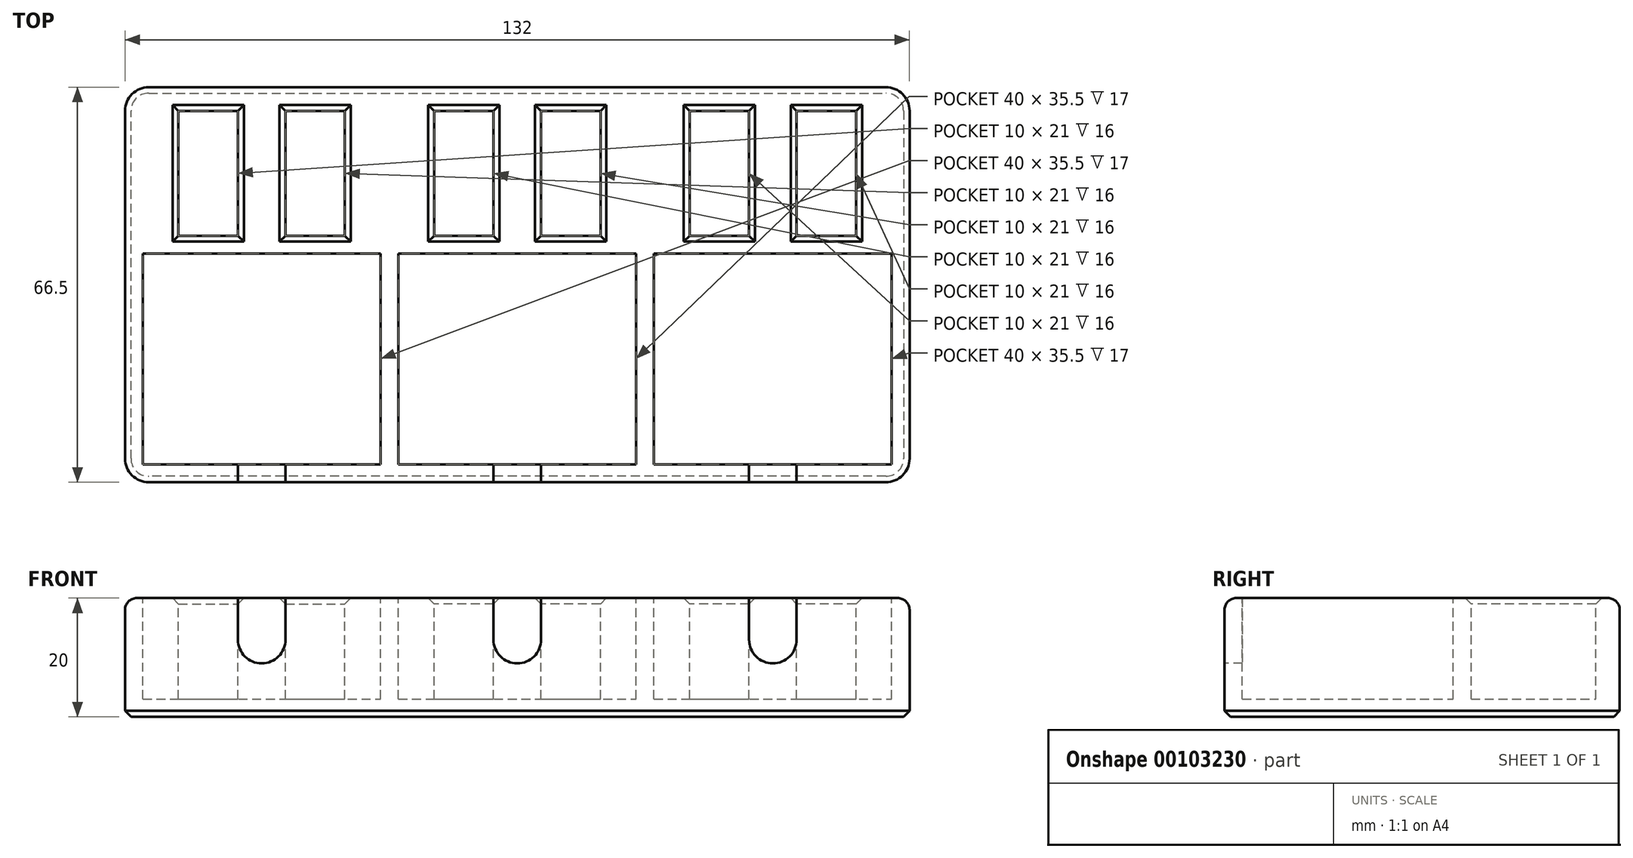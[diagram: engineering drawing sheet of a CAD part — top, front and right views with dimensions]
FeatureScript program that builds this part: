
annotation { "Feature Type Name" : "Feature", "Feature Type Description" : "" }
export const myFeature = defineFeature(function(context is Context, id is Id, definition is map)
    precondition{}
    {
        {
            var Q0;
            Q0=qCreatedBy(makeId("Top.planeOp"),FACE);
            var sketch = newSketch(context, id + "F0", { "sketchPlane" : qUnion([Q0])});
            skLineSegment(sketch, "E0.bottom", {"start": v(-67.44, -14.2) * mm, "end": v(-57.44, -14.2) * mm});
            skLineSegment(sketch, "E0.top", {"start": v(-67.44, -35.2) * mm, "end": v(-57.44, -35.2) * mm});
            skLineSegment(sketch, "E0.left", {"start": v(-67.44, -14.2) * mm, "end": v(-67.44, -35.2) * mm});
            skLineSegment(sketch, "E0.right", {"start": v(-57.44, -14.2) * mm, "end": v(-57.44, -35.2) * mm});
            skLineSegment(sketch, "E1.bottom", {"start": v(-73.44, 24.3) * mm, "end": v(-33.44, 24.3) * mm});
            skLineSegment(sketch, "E1.top", {"start": v(-73.44, -11.2) * mm, "end": v(-33.44, -11.2) * mm});
            skLineSegment(sketch, "E1.left", {"start": v(-73.44, 24.3) * mm, "end": v(-73.44, -11.2) * mm});
            skLineSegment(sketch, "E1.right", {"start": v(-33.44, 24.3) * mm, "end": v(-33.44, -11.2) * mm});
            skLineSegment(sketch, "E2", {"start": v(-53.44, 24.3) * mm, "end": v(-53.44, -11.2) * mm, "construction": true});
            skLineSegment(sketch, "E3", {"start": v(-62.44, -14.2) * mm, "end": v(-62.44, -35.2) * mm, "construction": true});
            skLineSegment(sketch, "E4", {"start": v(-62.44, 24.3) * mm, "end": v(-62.44, -11.2) * mm, "construction": true});
            skLineSegment(sketch, "E5", {"start": v(-44.44, 24.3) * mm, "end": v(-44.44, -11.2) * mm, "construction": true});
            skLineSegment(sketch, "E6", {"start": v(-62.44, -11.2) * mm, "end": v(-62.44, -14.2) * mm, "construction": true});
            skLineSegment(sketch, "E7", {"start": v(-44.44, -11.2) * mm, "end": v(-44.44, -14.2) * mm, "construction": true});
            skLineSegment(sketch, "E8.bottom", {"start": v(-49.44, -14.2) * mm, "end": v(-39.44, -14.2) * mm});
            skLineSegment(sketch, "E8.top", {"start": v(-49.44, -35.2) * mm, "end": v(-39.44, -35.2) * mm});
            skLineSegment(sketch, "E8.left", {"start": v(-49.44, -14.2) * mm, "end": v(-49.44, -35.2) * mm});
            skLineSegment(sketch, "E8.right", {"start": v(-39.44, -14.2) * mm, "end": v(-39.44, -35.2) * mm});
            skLineSegment(sketch, "E9", {"start": v(-44.44, -35.2) * mm, "end": v(-44.44, -14.2) * mm, "construction": true});
            skLineSegment(sketch, "E10.1.0.0", {"start": v(3.56, -14.2) * mm, "end": v(3.56, -35.2) * mm});
            skLineSegment(sketch, "E10.1.0.1", {"start": v(-10.44, 24.3) * mm, "end": v(-10.44, -11.2) * mm, "construction": true});
            skLineSegment(sketch, "E10.1.0.2", {"start": v(9.56, 24.3) * mm, "end": v(9.56, -11.2) * mm});
            skLineSegment(sketch, "E10.1.0.3", {"start": v(-1.44, -35.2) * mm, "end": v(-1.44, -14.2) * mm, "construction": true});
            skLineSegment(sketch, "E10.1.0.4", {"start": v(-1.44, 24.3) * mm, "end": v(-1.44, -11.2) * mm, "construction": true});
            skLineSegment(sketch, "E10.1.0.5", {"start": v(-19.44, 24.3) * mm, "end": v(-19.44, -11.2) * mm, "construction": true});
            skLineSegment(sketch, "E10.1.0.6", {"start": v(-6.44, -14.2) * mm, "end": v(-6.44, -35.2) * mm});
            skLineSegment(sketch, "E10.1.0.7", {"start": v(-30.44, -11.2) * mm, "end": v(9.56, -11.2) * mm});
            skLineSegment(sketch, "E10.1.0.8", {"start": v(-30.44, 24.3) * mm, "end": v(-30.44, -11.2) * mm});
            skLineSegment(sketch, "E10.1.0.9", {"start": v(-14.44, -14.2) * mm, "end": v(-14.44, -35.2) * mm});
            skLineSegment(sketch, "E10.1.0.10", {"start": v(-24.44, -14.2) * mm, "end": v(-24.44, -35.2) * mm});
            skLineSegment(sketch, "E10.1.0.11", {"start": v(-30.44, 24.3) * mm, "end": v(9.56, 24.3) * mm});
            skLineSegment(sketch, "E10.1.0.12", {"start": v(-19.44, -14.2) * mm, "end": v(-19.44, -35.2) * mm, "construction": true});
            skLineSegment(sketch, "E10.1.0.13", {"start": v(-6.44, -35.2) * mm, "end": v(3.56, -35.2) * mm});
            skLineSegment(sketch, "E10.1.0.14", {"start": v(-24.44, -35.2) * mm, "end": v(-14.44, -35.2) * mm});
            skLineSegment(sketch, "E10.1.0.15", {"start": v(-1.44, -11.2) * mm, "end": v(-1.44, -14.2) * mm, "construction": true});
            skLineSegment(sketch, "E10.1.0.16", {"start": v(-19.44, -11.2) * mm, "end": v(-19.44, -14.2) * mm, "construction": true});
            skLineSegment(sketch, "E10.1.0.17", {"start": v(-6.44, -14.2) * mm, "end": v(3.56, -14.2) * mm});
            skLineSegment(sketch, "E10.1.0.18", {"start": v(-24.44, -14.2) * mm, "end": v(-14.44, -14.2) * mm});
            skLineSegment(sketch, "E10.2.0.0", {"start": v(46.56, -14.2) * mm, "end": v(46.56, -35.2) * mm});
            skLineSegment(sketch, "E10.2.0.1", {"start": v(32.56, 24.3) * mm, "end": v(32.56, -11.2) * mm, "construction": true});
            skLineSegment(sketch, "E10.2.0.2", {"start": v(52.56, 24.3) * mm, "end": v(52.56, -11.2) * mm});
            skLineSegment(sketch, "E10.2.0.3", {"start": v(41.56, -35.2) * mm, "end": v(41.56, -14.2) * mm, "construction": true});
            skLineSegment(sketch, "E10.2.0.4", {"start": v(41.56, 24.3) * mm, "end": v(41.56, -11.2) * mm, "construction": true});
            skLineSegment(sketch, "E10.2.0.5", {"start": v(23.56, 24.3) * mm, "end": v(23.56, -11.2) * mm, "construction": true});
            skLineSegment(sketch, "E10.2.0.6", {"start": v(36.56, -14.2) * mm, "end": v(36.56, -35.2) * mm});
            skLineSegment(sketch, "E10.2.0.7", {"start": v(12.56, -11.2) * mm, "end": v(52.56, -11.2) * mm});
            skLineSegment(sketch, "E10.2.0.8", {"start": v(12.56, 24.3) * mm, "end": v(12.56, -11.2) * mm});
            skLineSegment(sketch, "E10.2.0.9", {"start": v(28.56, -14.2) * mm, "end": v(28.56, -35.2) * mm});
            skLineSegment(sketch, "E10.2.0.10", {"start": v(18.56, -14.2) * mm, "end": v(18.56, -35.2) * mm});
            skLineSegment(sketch, "E10.2.0.11", {"start": v(12.56, 24.3) * mm, "end": v(52.56, 24.3) * mm});
            skLineSegment(sketch, "E10.2.0.12", {"start": v(23.56, -14.2) * mm, "end": v(23.56, -35.2) * mm, "construction": true});
            skLineSegment(sketch, "E10.2.0.13", {"start": v(36.56, -35.2) * mm, "end": v(46.56, -35.2) * mm});
            skLineSegment(sketch, "E10.2.0.14", {"start": v(18.56, -35.2) * mm, "end": v(28.56, -35.2) * mm});
            skLineSegment(sketch, "E10.2.0.15", {"start": v(41.56, -11.2) * mm, "end": v(41.56, -14.2) * mm, "construction": true});
            skLineSegment(sketch, "E10.2.0.16", {"start": v(23.56, -11.2) * mm, "end": v(23.56, -14.2) * mm, "construction": true});
            skLineSegment(sketch, "E10.2.0.17", {"start": v(36.56, -14.2) * mm, "end": v(46.56, -14.2) * mm});
            skLineSegment(sketch, "E10.2.0.18", {"start": v(18.56, -14.2) * mm, "end": v(28.56, -14.2) * mm});
            skLineSegment(sketch, "E10.direction1", {"start": v(-39.44, -35.2) * mm, "end": v(3.56, -35.2) * mm, "construction": true});
            skLineSegment(sketch, "E11.bottom", {"start": v(-76.44, 27.3) * mm, "end": v(55.56, 27.3) * mm});
            skLineSegment(sketch, "E11.top", {"start": v(-76.44, -39.2) * mm, "end": v(55.56, -39.2) * mm});
            skLineSegment(sketch, "E11.left", {"start": v(-76.44, 27.3) * mm, "end": v(-76.44, -39.2) * mm});
            skLineSegment(sketch, "E11.right", {"start": v(55.56, 27.3) * mm, "end": v(55.56, -39.2) * mm});
            skSolve(sketch);
        }
        {
            var Q0;
            Q0=makeQuery(id+"F0.imprint","IMPRINT",FACE,{"disambiguationData":[TD([[makeQuery(id+"F0.imprint","IMPRINT",EDGE,{"derivedFrom":sQuery(id+"F0.wireOp",EDGE,"E0.bottom")}),1.0]])]});
            extrude(context, id + "F1", {"entities" : qUnion([Q0]), "depth" : 17 * mm});
        }
        {
            var Q0;
            Q0=makeQuery(id+"F1.opExtrude","CAP_FACE",FACE,{"disambiguationData":[OSD([sQuery(id+"F0.wireOp",EDGE,"E0.bottom"),sQuery(id+"F0.wireOp",EDGE,"E0.top"),sQuery(id+"F0.wireOp",EDGE,"E0.left"),sQuery(id+"F0.wireOp",EDGE,"E0.right"),sQuery(id+"F0.wireOp",EDGE,"E1.bottom"),sQuery(id+"F0.wireOp",EDGE,"E1.top"),sQuery(id+"F0.wireOp",EDGE,"E1.left"),sQuery(id+"F0.wireOp",EDGE,"E1.right"),sQuery(id+"F0.wireOp",EDGE,"E8.bottom"),sQuery(id+"F0.wireOp",EDGE,"E8.top"),sQuery(id+"F0.wireOp",EDGE,"E8.left"),sQuery(id+"F0.wireOp",EDGE,"E8.right"),sQuery(id+"F0.wireOp",EDGE,"E10.1.0.0"),sQuery(id+"F0.wireOp",EDGE,"E10.1.0.2"),sQuery(id+"F0.wireOp",EDGE,"E10.1.0.6"),sQuery(id+"F0.wireOp",EDGE,"E10.1.0.7"),sQuery(id+"F0.wireOp",EDGE,"E10.1.0.8"),sQuery(id+"F0.wireOp",EDGE,"E10.1.0.9"),sQuery(id+"F0.wireOp",EDGE,"E10.1.0.10"),sQuery(id+"F0.wireOp",EDGE,"E10.1.0.11"),sQuery(id+"F0.wireOp",EDGE,"E10.1.0.13"),sQuery(id+"F0.wireOp",EDGE,"E10.1.0.14"),sQuery(id+"F0.wireOp",EDGE,"E10.1.0.17"),sQuery(id+"F0.wireOp",EDGE,"E10.1.0.18"),sQuery(id+"F0.wireOp",EDGE,"E10.2.0.0"),sQuery(id+"F0.wireOp",EDGE,"E10.2.0.2"),sQuery(id+"F0.wireOp",EDGE,"E10.2.0.6"),sQuery(id+"F0.wireOp",EDGE,"E10.2.0.7"),sQuery(id+"F0.wireOp",EDGE,"E10.2.0.8"),sQuery(id+"F0.wireOp",EDGE,"E10.2.0.9"),sQuery(id+"F0.wireOp",EDGE,"E10.2.0.10"),sQuery(id+"F0.wireOp",EDGE,"E10.2.0.11"),sQuery(id+"F0.wireOp",EDGE,"E10.2.0.13"),sQuery(id+"F0.wireOp",EDGE,"E10.2.0.14"),sQuery(id+"F0.wireOp",EDGE,"E10.2.0.17"),sQuery(id+"F0.wireOp",EDGE,"E10.2.0.18"),sQuery(id+"F0.wireOp",EDGE,"E11.bottom"),sQuery(id+"F0.wireOp",EDGE,"E11.top"),sQuery(id+"F0.wireOp",EDGE,"E11.left"),sQuery(id+"F0.wireOp",EDGE,"E11.right")])],"isStart":false});
            var sketch = newSketch(context, id + "F2", { "sketchPlane" : qUnion([Q0])});
            skLineSegment(sketch, "E12.bottom", {"start": v(-76.44, 27.3) * mm, "end": v(55.56, 27.3) * mm});
            skLineSegment(sketch, "E12.top", {"start": v(-76.44, -39.2) * mm, "end": v(55.56, -39.2) * mm});
            skLineSegment(sketch, "E12.left", {"start": v(-76.44, 27.3) * mm, "end": v(-76.44, -39.2) * mm});
            skLineSegment(sketch, "E12.right", {"start": v(55.56, 27.3) * mm, "end": v(55.56, -39.2) * mm});
            skSolve(sketch);
        }
        {
            var Q0;
            Q0=makeQuery(id+"F2.imprint","IMPRINT",FACE,{"disambiguationData":[TD([[makeQuery(id+"F2.imprint","IMPRINT",EDGE,{"derivedFrom":sQuery(id+"F2.wireOp",EDGE,"E12.bottom")}),-1.0]])]});
            var Q1;
            Q1=makeQuery(id+"F2.imprint","IMPRINT",FACE,{"disambiguationData":[TD([[makeQuery(id+"F2.imprint","IMPRINT",EDGE,{"derivedFrom":makeQuery(id+"F1.opExtrude","CAP_EDGE",EDGE,{"disambiguationData":[OSD([sQuery(id+"F0.wireOp",EDGE,"E1.bottom")])],"isStart":false})}),-1.0]])]});
            var Q2;
            Q2=makeQuery(id+"F2.imprint","IMPRINT",FACE,{"disambiguationData":[TD([[makeQuery(id+"F2.imprint","IMPRINT",EDGE,{"derivedFrom":makeQuery(id+"F1.opExtrude","CAP_EDGE",EDGE,{"disambiguationData":[OSD([sQuery(id+"F0.wireOp",EDGE,"E10.1.0.2")])],"isStart":false})}),-1.0]])]});
            var Q3;
            Q3=makeQuery(id+"F2.imprint","IMPRINT",FACE,{"disambiguationData":[TD([[makeQuery(id+"F2.imprint","IMPRINT",EDGE,{"derivedFrom":makeQuery(id+"F1.opExtrude","CAP_EDGE",EDGE,{"disambiguationData":[OSD([sQuery(id+"F0.wireOp",EDGE,"E10.2.0.2")])],"isStart":false})}),-1.0]])]});
            var Q4;
            Q4=makeQuery(id+"F2.imprint","IMPRINT",FACE,{"disambiguationData":[TD([[makeQuery(id+"F2.imprint","IMPRINT",EDGE,{"derivedFrom":makeQuery(id+"F1.opExtrude","CAP_EDGE",EDGE,{"disambiguationData":[OSD([sQuery(id+"F0.wireOp",EDGE,"E10.2.0.0")])],"isStart":false})}),-1.0]])]});
            var Q5;
            Q5=makeQuery(id+"F2.imprint","IMPRINT",FACE,{"disambiguationData":[TD([[makeQuery(id+"F2.imprint","IMPRINT",EDGE,{"derivedFrom":makeQuery(id+"F1.opExtrude","CAP_EDGE",EDGE,{"disambiguationData":[OSD([sQuery(id+"F0.wireOp",EDGE,"E10.2.0.9")])],"isStart":false})}),-1.0]])]});
            var Q6;
            Q6=makeQuery(id+"F2.imprint","IMPRINT",FACE,{"disambiguationData":[TD([[makeQuery(id+"F2.imprint","IMPRINT",EDGE,{"derivedFrom":makeQuery(id+"F1.opExtrude","CAP_EDGE",EDGE,{"disambiguationData":[OSD([sQuery(id+"F0.wireOp",EDGE,"E10.1.0.0")])],"isStart":false})}),-1.0]])]});
            var Q7;
            Q7=makeQuery(id+"F2.imprint","IMPRINT",FACE,{"disambiguationData":[TD([[makeQuery(id+"F2.imprint","IMPRINT",EDGE,{"derivedFrom":makeQuery(id+"F1.opExtrude","CAP_EDGE",EDGE,{"disambiguationData":[OSD([sQuery(id+"F0.wireOp",EDGE,"E10.1.0.9")])],"isStart":false})}),-1.0]])]});
            var Q8;
            Q8=makeQuery(id+"F2.imprint","IMPRINT",FACE,{"disambiguationData":[TD([[makeQuery(id+"F2.imprint","IMPRINT",EDGE,{"derivedFrom":makeQuery(id+"F1.opExtrude","CAP_EDGE",EDGE,{"disambiguationData":[OSD([sQuery(id+"F0.wireOp",EDGE,"E8.bottom")])],"isStart":false})}),-1.0]])]});
            var Q9;
            Q9=makeQuery(id+"F2.imprint","IMPRINT",FACE,{"disambiguationData":[TD([[makeQuery(id+"F2.imprint","IMPRINT",EDGE,{"derivedFrom":makeQuery(id+"F1.opExtrude","CAP_EDGE",EDGE,{"disambiguationData":[OSD([sQuery(id+"F0.wireOp",EDGE,"E0.bottom")])],"isStart":false})}),-1.0]])]});
            extrude(context, id + "F3", {"entities" : qUnion([Q0, Q1, Q2, Q3, Q4, Q5, Q6, Q7, Q8, Q9]), "operationType" : NewBodyOperationType.ADD, "depth" : 3 * mm});
        }
        {
            var Q0;
            Q0=makeQuery(id+"F3.boolean.opBoolean","MERGE",FACE,{"derivedFrom":[makeQuery(id+"F1.opExtrude","SWEPT_FACE",FACE,{"disambiguationData":[OSD([sQuery(id+"F0.wireOp",EDGE,"E11.bottom")])]}),makeQuery(id+"F3.opExtrude","SWEPT_FACE",FACE,{"disambiguationData":[OSD([sQuery(id+"F2.wireOp",EDGE,"E12.bottom")])]})]});
            var sketch = newSketch(context, id + "F4", { "sketchPlane" : qUnion([Q0])});
            skLineSegment(sketch, "E13.0", {"start": v(73.44, 17) * mm, "end": v(33.44, 17) * mm, "construction": true});
            skLineSegment(sketch, "E13.1", {"start": v(30.44, 17) * mm, "end": v(-9.56, 17) * mm, "construction": true});
            skLineSegment(sketch, "E13.2", {"start": v(-12.56, 17) * mm, "end": v(-52.56, 17) * mm, "construction": true});
            skLineSegment(sketch, "E14", {"start": v(53.44, 17) * mm, "end": v(53.44, 0) * mm, "construction": true});
            skLineSegment(sketch, "E15", {"start": v(10.44, 17) * mm, "end": v(10.44, 0) * mm, "construction": true});
            skLineSegment(sketch, "E16", {"start": v(-32.56, 17) * mm, "end": v(-32.56, 0) * mm, "construction": true});
            skArc(sketch, "E17", {"start": v(57.44, 7) * mm, "mid": v(53.44, 11) * mm, "end": v(49.44, 7) * mm});
            skArc(sketch, "E18", {"start": v(14.44, 7) * mm, "mid": v(10.44, 11) * mm, "end": v(6.44, 7) * mm});
            skArc(sketch, "E19", {"start": v(-28.56, 7) * mm, "mid": v(-32.56, 11) * mm, "end": v(-36.56, 7) * mm});
            skLineSegment(sketch, "E20", {"start": v(52.02, 11) * mm, "end": v(-51.4, 11) * mm, "construction": true});
            skLineSegment(sketch, "E21", {"start": v(57.44, 7) * mm, "end": v(57.44, 0) * mm});
            skLineSegment(sketch, "E22", {"start": v(49.44, 7) * mm, "end": v(49.44, 0) * mm});
            skLineSegment(sketch, "E23", {"start": v(14.44, 7) * mm, "end": v(14.44, 0) * mm});
            skLineSegment(sketch, "E24", {"start": v(6.44, 7) * mm, "end": v(6.44, 0) * mm});
            skLineSegment(sketch, "E25", {"start": v(-28.56, 7) * mm, "end": v(-28.56, 0) * mm});
            skLineSegment(sketch, "E26", {"start": v(-36.56, 7) * mm, "end": v(-36.56, 0) * mm});
            skSolve(sketch);
        }
        {
            var Q0;
            Q0=makeQuery(id+"F4.imprint","IMPRINT",FACE,{"disambiguationData":[TD([[makeQuery(id+"F4.imprint","IMPRINT",EDGE,{"derivedFrom":sQuery(id+"F4.wireOp",EDGE,"E17")}),1.0]])]});
            var Q1;
            Q1=makeQuery(id+"F4.imprint","IMPRINT",FACE,{"disambiguationData":[TD([[makeQuery(id+"F4.imprint","IMPRINT",EDGE,{"derivedFrom":sQuery(id+"F4.wireOp",EDGE,"E18")}),1.0]])]});
            var Q2;
            Q2=makeQuery(id+"F4.imprint","IMPRINT",FACE,{"disambiguationData":[TD([[makeQuery(id+"F4.imprint","IMPRINT",EDGE,{"derivedFrom":sQuery(id+"F4.wireOp",EDGE,"E19")}),1.0]])]});
            var Q3;
            Q3=makeQuery(id+"F1.opExtrude","SWEPT_FACE",FACE,{"disambiguationData":[OSD([sQuery(id+"F0.wireOp",EDGE,"E1.bottom")])]});
            extrude(context, id + "F5", {"entities" : qUnion([Q0, Q1, Q2]), "operationType" : NewBodyOperationType.REMOVE, "endBound" : BoundingType.UP_TO_SURFACE, "oppositeDirection" : true, "endBoundEntityFace" : qUnion([Q3]), "depth" : 25 * mm});
        }
        {
            var Q0;
            Q0=makeQuery(id+"F1.opExtrude","SWEPT_BODY",BODY,{"disambiguationData":[OSD([sQuery(id+"F0.wireOp",EDGE,"E0.bottom"),sQuery(id+"F0.wireOp",EDGE,"E0.top"),sQuery(id+"F0.wireOp",EDGE,"E0.left"),sQuery(id+"F0.wireOp",EDGE,"E0.right"),sQuery(id+"F0.wireOp",EDGE,"E1.bottom"),sQuery(id+"F0.wireOp",EDGE,"E1.top"),sQuery(id+"F0.wireOp",EDGE,"E1.left"),sQuery(id+"F0.wireOp",EDGE,"E1.right"),sQuery(id+"F0.wireOp",EDGE,"E8.bottom"),sQuery(id+"F0.wireOp",EDGE,"E8.top"),sQuery(id+"F0.wireOp",EDGE,"E8.left"),sQuery(id+"F0.wireOp",EDGE,"E8.right"),sQuery(id+"F0.wireOp",EDGE,"E10.1.0.0"),sQuery(id+"F0.wireOp",EDGE,"E10.1.0.2"),sQuery(id+"F0.wireOp",EDGE,"E10.1.0.6"),sQuery(id+"F0.wireOp",EDGE,"E10.1.0.7"),sQuery(id+"F0.wireOp",EDGE,"E10.1.0.8"),sQuery(id+"F0.wireOp",EDGE,"E10.1.0.9"),sQuery(id+"F0.wireOp",EDGE,"E10.1.0.10"),sQuery(id+"F0.wireOp",EDGE,"E10.1.0.11"),sQuery(id+"F0.wireOp",EDGE,"E10.1.0.13"),sQuery(id+"F0.wireOp",EDGE,"E10.1.0.14"),sQuery(id+"F0.wireOp",EDGE,"E10.1.0.17"),sQuery(id+"F0.wireOp",EDGE,"E10.1.0.18"),sQuery(id+"F0.wireOp",EDGE,"E10.2.0.0"),sQuery(id+"F0.wireOp",EDGE,"E10.2.0.2"),sQuery(id+"F0.wireOp",EDGE,"E10.2.0.6"),sQuery(id+"F0.wireOp",EDGE,"E10.2.0.7"),sQuery(id+"F0.wireOp",EDGE,"E10.2.0.8"),sQuery(id+"F0.wireOp",EDGE,"E10.2.0.9"),sQuery(id+"F0.wireOp",EDGE,"E10.2.0.10"),sQuery(id+"F0.wireOp",EDGE,"E10.2.0.11"),sQuery(id+"F0.wireOp",EDGE,"E10.2.0.13"),sQuery(id+"F0.wireOp",EDGE,"E10.2.0.14"),sQuery(id+"F0.wireOp",EDGE,"E10.2.0.17"),sQuery(id+"F0.wireOp",EDGE,"E10.2.0.18"),sQuery(id+"F0.wireOp",EDGE,"E11.bottom"),sQuery(id+"F0.wireOp",EDGE,"E11.top"),sQuery(id+"F0.wireOp",EDGE,"E11.left"),sQuery(id+"F0.wireOp",EDGE,"E11.right")])]});
            var Q1;
            Q1=makeQuery(id+"F3.opExtrude","CAP_EDGE",EDGE,{"disambiguationData":[OSD([sQuery(id+"F2.wireOp",EDGE,"E12.bottom")])],"isStart":false});
            transform(context, id + "F6", {"entities" : qUnion([Q0]), "transformType" : TransformType.ROTATION, "transformAxis" : qUnion([Q1]), "angle" : 180 * degree, "makeCopy" : false});
        }
        {
            var Q0;
            Q0=makeQuery(id+"F3.boolean.opBoolean","MERGE",EDGE,{"derivedFrom":[makeQuery(id+"F1.opExtrude","SWEPT_EDGE",EDGE,{"disambiguationData":[OSD([sQuery(id+"F0.wireOp",EDGE,"E11.bottom"),sQuery(id+"F0.wireOp",EDGE,"E11.left")])]}),makeQuery(id+"F3.opExtrude","SWEPT_EDGE",EDGE,{"disambiguationData":[OSD([sQuery(id+"F2.wireOp",EDGE,"E12.bottom"),sQuery(id+"F2.wireOp",EDGE,"E12.left")])]})]});
            var Q1;
            Q1=makeQuery(id+"F3.boolean.opBoolean","MERGE",EDGE,{"derivedFrom":[makeQuery(id+"F1.opExtrude","SWEPT_EDGE",EDGE,{"disambiguationData":[OSD([sQuery(id+"F0.wireOp",EDGE,"E11.bottom"),sQuery(id+"F0.wireOp",EDGE,"E11.right")])]}),makeQuery(id+"F3.opExtrude","SWEPT_EDGE",EDGE,{"disambiguationData":[OSD([sQuery(id+"F2.wireOp",EDGE,"E12.bottom"),sQuery(id+"F2.wireOp",EDGE,"E12.right")])]})]});
            var Q2;
            Q2=makeQuery(id+"F3.boolean.opBoolean","MERGE",EDGE,{"derivedFrom":[makeQuery(id+"F1.opExtrude","SWEPT_EDGE",EDGE,{"disambiguationData":[OSD([sQuery(id+"F0.wireOp",EDGE,"E11.top"),sQuery(id+"F0.wireOp",EDGE,"E11.right")])]}),makeQuery(id+"F3.opExtrude","SWEPT_EDGE",EDGE,{"disambiguationData":[OSD([sQuery(id+"F2.wireOp",EDGE,"E12.top"),sQuery(id+"F2.wireOp",EDGE,"E12.right")])]})]});
            var Q3;
            Q3=makeQuery(id+"F3.boolean.opBoolean","MERGE",EDGE,{"derivedFrom":[makeQuery(id+"F1.opExtrude","SWEPT_EDGE",EDGE,{"disambiguationData":[OSD([sQuery(id+"F0.wireOp",EDGE,"E11.top"),sQuery(id+"F0.wireOp",EDGE,"E11.left")])]}),makeQuery(id+"F3.opExtrude","SWEPT_EDGE",EDGE,{"disambiguationData":[OSD([sQuery(id+"F2.wireOp",EDGE,"E12.top"),sQuery(id+"F2.wireOp",EDGE,"E12.left")])]})]});
            fillet(context, id + "F7", {"entities" : qUnion([Q0, Q1, Q2, Q3]), "radius" : 4 * mm, "tangentPropagation" : true, "allowEdgeOverflow" : false});
        }
        {
            var Q0;
            Q0=makeQuery(id+"F1.opExtrude","CAP_EDGE",EDGE,{"disambiguationData":[OSD([sQuery(id+"F0.wireOp",EDGE,"E11.left")])],"isStart":true});
            var Q1;
            Q1=makeQuery(id+"F1.opExtrude","CAP_EDGE",EDGE,{"disambiguationData":[OSD([sQuery(id+"F0.wireOp",EDGE,"E11.top")])],"isStart":true});
            var Q2;
            {var subQ0=sQuery(id+"F0.wireOp",EDGE,"E11.bottom");Q2=makeQuery(id+"F5.boolean.opBoolean","SPLIT",EDGE,{"disambiguationData":[TD([makeQuery(id+"F5.opExtrude","SWEPT_FACE",FACE,{"disambiguationData":[OSD([sQuery(id+"F4.wireOp",EDGE,"E22")])]})])],"derivedFrom":makeQuery(id+"F1.opExtrude","CAP_EDGE",EDGE,{"disambiguationData":[OSD([subQ0])],"isStart":true})});}
            var Q3;
            {var subQ0=sQuery(id+"F0.wireOp",EDGE,"E11.bottom");Q3=makeQuery(id+"F5.boolean.opBoolean","SPLIT",EDGE,{"disambiguationData":[TD([makeQuery(id+"F5.opExtrude","SWEPT_FACE",FACE,{"disambiguationData":[OSD([sQuery(id+"F4.wireOp",EDGE,"E24")])]})])],"derivedFrom":makeQuery(id+"F1.opExtrude","CAP_EDGE",EDGE,{"disambiguationData":[OSD([subQ0])],"isStart":true})});}
            fillet(context, id + "F8", {"entities" : qUnion([Q0, Q1, Q2, Q3]), "radius" : 2 * mm, "tangentPropagation" : true, "allowEdgeOverflow" : false});
        }
        {
            var Q0;
            Q0=makeQuery(id+"F1.opExtrude","CAP_EDGE",EDGE,{"disambiguationData":[OSD([sQuery(id+"F0.wireOp",EDGE,"E0.left")])],"isStart":true});
            var Q1;
            Q1=makeQuery(id+"F1.opExtrude","CAP_EDGE",EDGE,{"disambiguationData":[OSD([sQuery(id+"F0.wireOp",EDGE,"E8.right")])],"isStart":true});
            var Q2;
            Q2=makeQuery(id+"F1.opExtrude","CAP_EDGE",EDGE,{"disambiguationData":[OSD([sQuery(id+"F0.wireOp",EDGE,"E8.left")])],"isStart":true});
            var Q3;
            Q3=makeQuery(id+"F1.opExtrude","CAP_EDGE",EDGE,{"disambiguationData":[OSD([sQuery(id+"F0.wireOp",EDGE,"E0.bottom")])],"isStart":true});
            var Q4;
            Q4=makeQuery(id+"F1.opExtrude","CAP_EDGE",EDGE,{"disambiguationData":[OSD([sQuery(id+"F0.wireOp",EDGE,"E0.right")])],"isStart":true});
            var Q5;
            Q5=makeQuery(id+"F1.opExtrude","CAP_EDGE",EDGE,{"disambiguationData":[OSD([sQuery(id+"F0.wireOp",EDGE,"E10.1.0.10")])],"isStart":true});
            var Q6;
            Q6=makeQuery(id+"F1.opExtrude","CAP_EDGE",EDGE,{"disambiguationData":[OSD([sQuery(id+"F0.wireOp",EDGE,"E10.1.0.9")])],"isStart":true});
            var Q7;
            Q7=makeQuery(id+"F1.opExtrude","CAP_EDGE",EDGE,{"disambiguationData":[OSD([sQuery(id+"F0.wireOp",EDGE,"E10.1.0.6")])],"isStart":true});
            var Q8;
            Q8=makeQuery(id+"F1.opExtrude","CAP_EDGE",EDGE,{"disambiguationData":[OSD([sQuery(id+"F0.wireOp",EDGE,"E10.1.0.0")])],"isStart":true});
            var Q9;
            Q9=makeQuery(id+"F1.opExtrude","CAP_EDGE",EDGE,{"disambiguationData":[OSD([sQuery(id+"F0.wireOp",EDGE,"E10.2.0.10")])],"isStart":true});
            var Q10;
            Q10=makeQuery(id+"F1.opExtrude","CAP_EDGE",EDGE,{"disambiguationData":[OSD([sQuery(id+"F0.wireOp",EDGE,"E10.2.0.9")])],"isStart":true});
            var Q11;
            Q11=makeQuery(id+"F1.opExtrude","CAP_EDGE",EDGE,{"disambiguationData":[OSD([sQuery(id+"F0.wireOp",EDGE,"E10.2.0.6")])],"isStart":true});
            var Q12;
            Q12=makeQuery(id+"F1.opExtrude","CAP_EDGE",EDGE,{"disambiguationData":[OSD([sQuery(id+"F0.wireOp",EDGE,"E10.2.0.0")])],"isStart":true});
            var Q13;
            Q13=makeQuery(id+"F1.opExtrude","CAP_EDGE",EDGE,{"disambiguationData":[OSD([sQuery(id+"F0.wireOp",EDGE,"E10.2.0.17")])],"isStart":true});
            var Q14;
            Q14=makeQuery(id+"F1.opExtrude","CAP_EDGE",EDGE,{"disambiguationData":[OSD([sQuery(id+"F0.wireOp",EDGE,"E10.2.0.18")])],"isStart":true});
            var Q15;
            Q15=makeQuery(id+"F1.opExtrude","CAP_EDGE",EDGE,{"disambiguationData":[OSD([sQuery(id+"F0.wireOp",EDGE,"E10.1.0.17")])],"isStart":true});
            var Q16;
            Q16=makeQuery(id+"F1.opExtrude","CAP_EDGE",EDGE,{"disambiguationData":[OSD([sQuery(id+"F0.wireOp",EDGE,"E10.1.0.18")])],"isStart":true});
            var Q17;
            Q17=makeQuery(id+"F1.opExtrude","CAP_EDGE",EDGE,{"disambiguationData":[OSD([sQuery(id+"F0.wireOp",EDGE,"E8.bottom")])],"isStart":true});
            var Q18;
            Q18=makeQuery(id+"F1.opExtrude","CAP_EDGE",EDGE,{"disambiguationData":[OSD([sQuery(id+"F0.wireOp",EDGE,"E8.top")])],"isStart":true});
            var Q19;
            Q19=makeQuery(id+"F1.opExtrude","CAP_EDGE",EDGE,{"disambiguationData":[OSD([sQuery(id+"F0.wireOp",EDGE,"E0.top")])],"isStart":true});
            var Q20;
            Q20=makeQuery(id+"F1.opExtrude","CAP_EDGE",EDGE,{"disambiguationData":[OSD([sQuery(id+"F0.wireOp",EDGE,"E10.1.0.14")])],"isStart":true});
            var Q21;
            Q21=makeQuery(id+"F1.opExtrude","CAP_EDGE",EDGE,{"disambiguationData":[OSD([sQuery(id+"F0.wireOp",EDGE,"E10.1.0.13")])],"isStart":true});
            var Q22;
            Q22=makeQuery(id+"F1.opExtrude","CAP_EDGE",EDGE,{"disambiguationData":[OSD([sQuery(id+"F0.wireOp",EDGE,"E10.2.0.14")])],"isStart":true});
            var Q23;
            Q23=makeQuery(id+"F1.opExtrude","CAP_EDGE",EDGE,{"disambiguationData":[OSD([sQuery(id+"F0.wireOp",EDGE,"E10.2.0.13")])],"isStart":true});
            chamfer(context, id + "F9", {"entities" : qUnion([Q0, Q1, Q2, Q3, Q4, Q5, Q6, Q7, Q8, Q9, Q10, Q11, Q12, Q13, Q14, Q15, Q16, Q17, Q18, Q19, Q20, Q21, Q22, Q23]), "width" : 1 * mm, "tangentPropagation" : true});
        }
        {
            var Q0;
            Q0=makeQuery(id+"F3.opExtrude","CAP_EDGE",EDGE,{"disambiguationData":[OSD([sQuery(id+"F2.wireOp",EDGE,"E12.bottom")])],"isStart":false});
            chamfer(context, id + "F10", {"entities" : qUnion([Q0]), "width" : 1 * mm, "tangentPropagation" : true});
        }
    });
